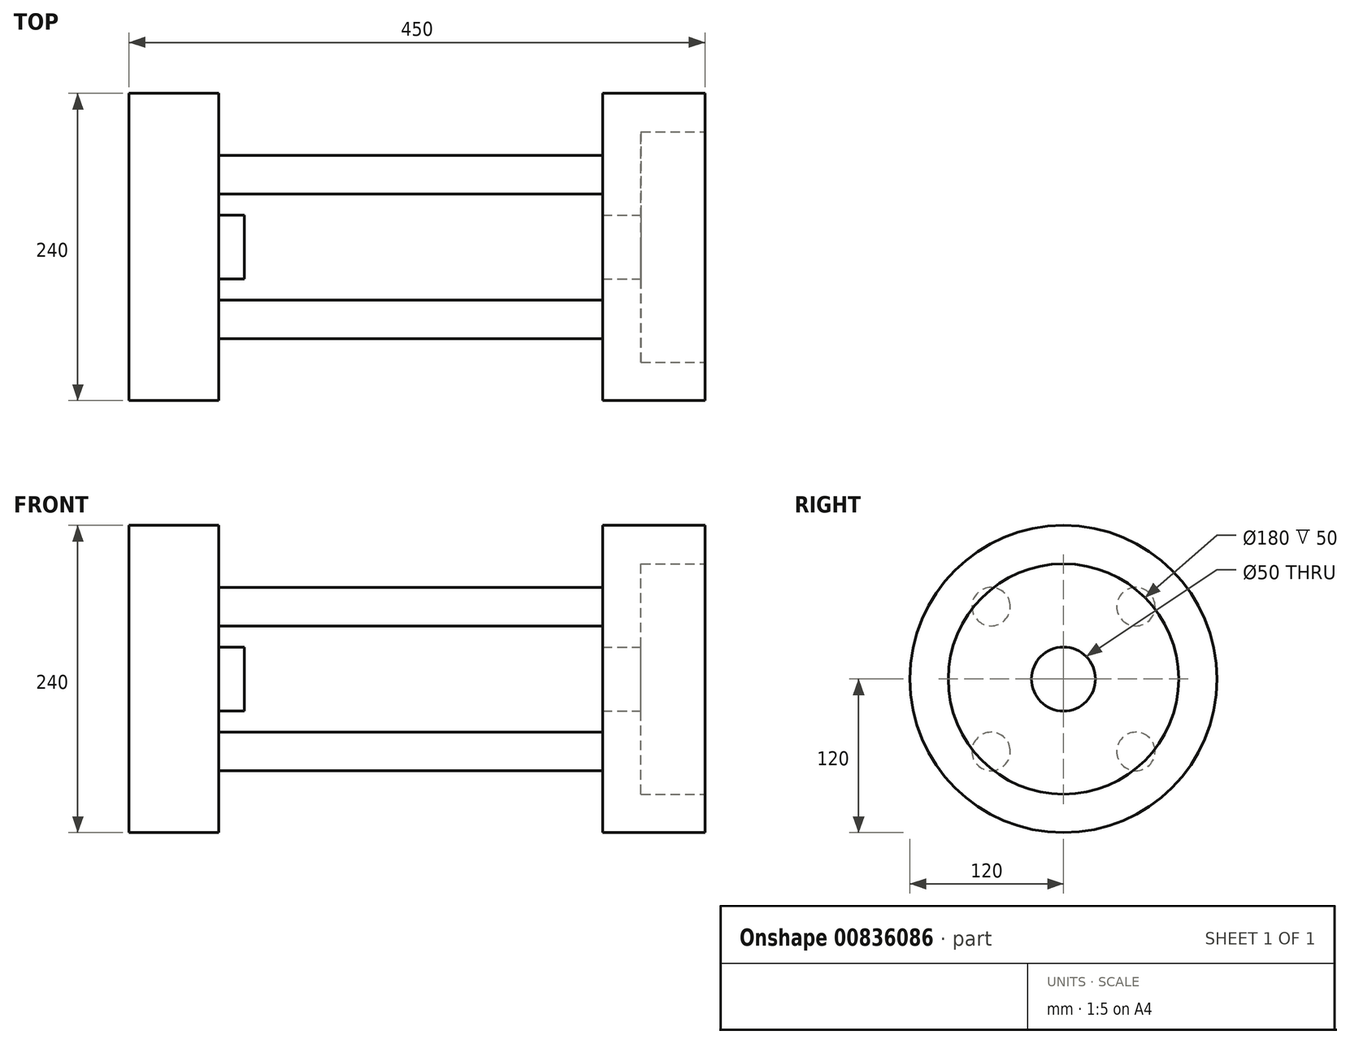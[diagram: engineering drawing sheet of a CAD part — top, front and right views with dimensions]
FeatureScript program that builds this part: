
annotation { "Feature Type Name" : "Feature", "Feature Type Description" : "" }
export const myFeature = defineFeature(function(context is Context, id is Id, definition is map)
    precondition{}
    {
        {
            var Q0;
            Q0=qCreatedBy(makeId("Right.planeOp"),FACE);
            var sketch = newSketch(context, id + "F0", { "sketchPlane" : qUnion([Q0])});
            skCircle(sketch, "E0", {"center": v(0, 0) * mm, "radius": 120 * mm});
            skSolve(sketch);
        }
        {
            var Q0;
            Q0 = qSketchRegion(id + "F0", true);
            extrude(context, id + "F1", {"entities" : qUnion([Q0]), "depth" : 70 * mm, "offsetDistance" : 25 * mm});
        }
        {
            var Q0;
            Q0=makeQuery(id+"F1.opExtrude","CAP_FACE",FACE,{"disambiguationData":[OSD([sQuery(id+"F0.wireOp",EDGE,"E0")])],"isStart":false});
            var sketch = newSketch(context, id + "F2", { "sketchPlane" : qUnion([Q0])});
            skCircle(sketch, "E1", {"center": v(0, 0) * mm, "radius": 25 * mm});
            skSolve(sketch);
        }
        {
            var Q0;
            Q0 = qSketchRegion(id + "F2", true);
            extrude(context, id + "F3", {"entities" : qUnion([Q0]), "operationType" : NewBodyOperationType.ADD, "depth" : 20 * mm, "offsetDistance" : 25 * mm});
        }
        {
            var Q0;
            Q0=makeQuery(id+"F1.opExtrude","CAP_FACE",FACE,{"disambiguationData":[OSD([sQuery(id+"F0.wireOp",EDGE,"E0")])],"isStart":false});
            var sketch = newSketch(context, id + "F4", { "sketchPlane" : qUnion([Q0])});
            skCircle(sketch, "E2", {"center": v(-56.57, 56.57) * mm, "radius": 15 * mm});
            skPoint(sketch, "E3.start.orphan", {"position": v(0, 0) * mm});
            skCircle(sketch, "E4.1.0", {"center": v(56.57, 56.57) * mm, "radius": 15 * mm});
            skCircle(sketch, "E4.2.0", {"center": v(56.57, -56.57) * mm, "radius": 15 * mm});
            skCircle(sketch, "E4.3.0", {"center": v(-56.57, -56.57) * mm, "radius": 15 * mm});
            skLineSegment(sketch, "E4.anchor1", {"start": v(0, 0) * mm, "end": v(-56.57, 56.57) * mm, "construction": true});
            skLineSegment(sketch, "E4.anchor2", {"start": v(0, 0) * mm, "end": v(-56.57, -56.57) * mm, "construction": true});
            skSolve(sketch);
        }
        {
            var Q0;
            Q0=makeQuery(id+"F4.imprint","IMPRINT",FACE,{"disambiguationData":[TD([[makeQuery(id+"F4.imprint","IMPRINT",EDGE,{"derivedFrom":sQuery(id+"F4.wireOp",EDGE,"E4.3.0")}),1.0]])]});
            var Q1;
            Q1=makeQuery(id+"F4.imprint","IMPRINT",FACE,{"disambiguationData":[TD([[makeQuery(id+"F4.imprint","IMPRINT",EDGE,{"derivedFrom":sQuery(id+"F4.wireOp",EDGE,"E2")}),1.0]])]});
            var Q2;
            Q2=makeQuery(id+"F4.imprint","IMPRINT",FACE,{"disambiguationData":[TD([[makeQuery(id+"F4.imprint","IMPRINT",EDGE,{"derivedFrom":sQuery(id+"F4.wireOp",EDGE,"E4.1.0")}),1.0]])]});
            var Q3;
            Q3=makeQuery(id+"F4.imprint","IMPRINT",FACE,{"disambiguationData":[TD([[makeQuery(id+"F4.imprint","IMPRINT",EDGE,{"derivedFrom":sQuery(id+"F4.wireOp",EDGE,"E4.2.0")}),1.0]])]});
            var Q4;
            Q4=sQuery(id+"F4.wireOp",EDGE,"E2");
            var Q5;
            Q5=sQuery(id+"F4.wireOp",EDGE,"E4.1.0");
            var Q6;
            Q6=sQuery(id+"F4.wireOp",EDGE,"E4.2.0");
            var Q7;
            Q7=sQuery(id+"F4.wireOp",EDGE,"E4.3.0");
            extrude(context, id + "F5", {"entities" : qUnion([Q0, Q1, Q2, Q3]), "surfaceEntities" : qUnion([Q4, Q5, Q6, Q7]), "depth" : 300 * mm, "offsetDistance" : 25 * mm});
        }
        {
            var Q0;
            Q0=makeQuery(id+"F5.opExtrude","CAP_FACE",FACE,{"disambiguationData":[OSD([sQuery(id+"F4.wireOp",EDGE,"E4.2.0")])],"isStart":false});
            var sketch = newSketch(context, id + "F6", { "sketchPlane" : qUnion([Q0])});
            skCircle(sketch, "E5", {"center": v(0, 0) * mm, "radius": 120 * mm});
            skSolve(sketch);
        }
        {
            var Q0;
            Q0 = qSketchRegion(id + "F6", true);
            extrude(context, id + "F7", {"entities" : qUnion([Q0]), "depth" : 80 * mm, "offsetDistance" : 25 * mm});
        }
        {
            var Q0;
            Q0=makeQuery(id+"F7.opExtrude","CAP_FACE",FACE,{"disambiguationData":[OSD([sQuery(id+"F6.wireOp",EDGE,"E5")])],"isStart":false});
            var sketch = newSketch(context, id + "F8", { "sketchPlane" : qUnion([Q0])});
            skCircle(sketch, "E6", {"center": v(0, 0) * mm, "radius": 90 * mm});
            skSolve(sketch);
        }
        {
            var Q0;
            Q0 = qSketchRegion(id + "F8", true);
            extrude(context, id + "F9", {"entities" : qUnion([Q0]), "operationType" : NewBodyOperationType.REMOVE, "oppositeDirection" : true, "depth" : 50 * mm, "offsetDistance" : 25 * mm});
        }
        {
            var Q0;
            Q0=makeQuery(id+"F9.boolean.opBoolean","COPY",FACE,{"derivedFrom":makeQuery(id+"F9.opExtrude","CAP_FACE",FACE,{"disambiguationData":[OSD([sQuery(id+"F8.wireOp",EDGE,"E6")])],"isStart":false})});
            var sketch = newSketch(context, id + "F10", { "sketchPlane" : qUnion([Q0])});
            skCircle(sketch, "E7", {"center": v(0, 0) * mm, "radius": 25 * mm});
            skSolve(sketch);
        }
        {
            var Q0;
            Q0 = qSketchRegion(id + "F10", true);
            extrude(context, id + "F11", {"entities" : qUnion([Q0]), "operationType" : NewBodyOperationType.REMOVE, "oppositeDirection" : true, "depth" : 60 * mm, "offsetDistance" : 25 * mm});
        }
    });
